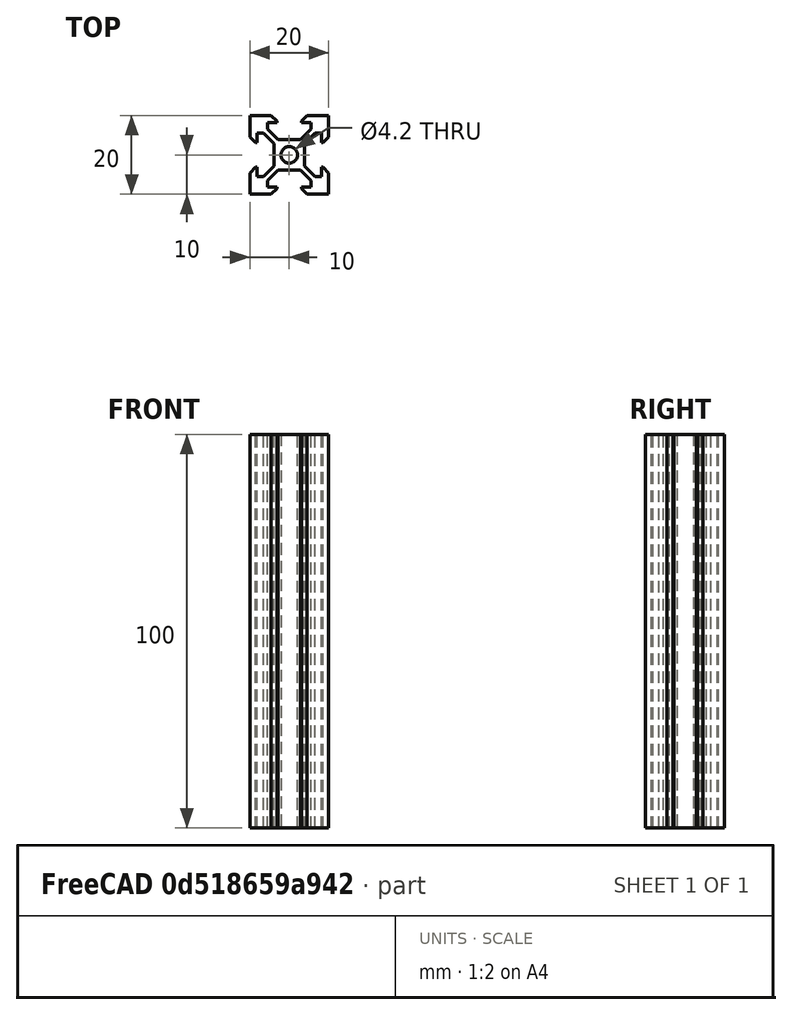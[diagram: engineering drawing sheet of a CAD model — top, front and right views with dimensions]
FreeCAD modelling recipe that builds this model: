
FCSTD DOCUMENT  (FreeCAD 2022.430R26244 +4758 (Git))
Label: V-Slot 2020-100
License: All rights reserved
LicenseURL: http://en.wikipedia.org/wiki/All_rights_reserved
objects: Sketcher::SketchObject×1, PartDesign::Pad×1, PartDesign::Body×1, App::Part×1
note: 5 computed .brp shape members not serialized (recipe doc carries the construction recipe); baked Part::Feature solids carry a one-line shape summary decoded from their .brp

FEATURE [Sketcher::SketchObject] Sketch
  FullyConstrained = true
  MapMode = 5
  Support = -> [XY_Plane001]
  TreeRank = 0
  sketch-geometry (59):
    g0: Circle CenterX=0 CenterY=0 CenterZ=0 NormalX=0 NormalY=0 NormalZ=1 AngleXU=0 Radius=2.1
    g1: LineSegment StartX=-10 StartY=10 StartZ=0 EndX=-4.58 EndY=10 EndZ=0
    g2: LineSegment StartX=10 StartY=10 StartZ=0 EndX=10 EndY=4.58 EndZ=0
    g3: LineSegment StartX=10 StartY=-10 StartZ=0 EndX=4.58 EndY=-10 EndZ=0
    g4: LineSegment StartX=-10 StartY=-10 StartZ=0 EndX=-10 EndY=-4.58 EndZ=0
    g5: LineSegment StartX=-5.5 StartY=6.56066 StartZ=0 EndX=-2.83934 EndY=3.9 EndZ=0
    g6: LineSegment StartX=-6.56066 StartY=5.5 StartZ=0 EndX=-3.9 EndY=2.83934 EndZ=0
    g7: LineSegment StartX=2.83934 StartY=3.9 StartZ=0 EndX=5.5 EndY=6.56066 EndZ=0
    g8: LineSegment StartX=3.9 StartY=2.83934 StartZ=0 EndX=6.56066 EndY=5.5 EndZ=0
    g9: LineSegment StartX=3.9 StartY=-2.83934 StartZ=0 EndX=6.56066 EndY=-5.5 EndZ=0
    g10: LineSegment StartX=2.83934 StartY=-3.9 StartZ=0 EndX=5.5 EndY=-6.56066 EndZ=0
    g11: LineSegment StartX=-2.83934 StartY=-3.9 StartZ=0 EndX=-5.5 EndY=-6.56066 EndZ=0
    g12: LineSegment StartX=-3.9 StartY=-2.83934 StartZ=0 EndX=-6.56066 EndY=-5.5 EndZ=0
    g13: LineSegment [constr] StartX=-10 StartY=10 StartZ=0 EndX=10 EndY=-10 EndZ=0
    g14: LineSegment [constr] StartX=-10 StartY=-10 StartZ=0 EndX=10 EndY=10 EndZ=0
    g15: LineSegment StartX=-2.83934 StartY=3.9 StartZ=0 EndX=2.83934 EndY=3.9 EndZ=0
    g16: LineSegment StartX=-3.9 StartY=2.83934 StartZ=0 EndX=-3.9 EndY=-2.83934 EndZ=0
    g17: LineSegment StartX=-2.83934 StartY=-3.9 StartZ=0 EndX=2.83934 EndY=-3.9 EndZ=0
    g18: LineSegment StartX=3.9 StartY=2.83934 StartZ=0 EndX=3.9 EndY=-2.83934 EndZ=0
    g19: LineSegment StartX=-5.5 StartY=6.56066 StartZ=0 EndX=-5.5 EndY=8.2 EndZ=0
    g20: LineSegment StartX=5.5 StartY=6.56066 StartZ=0 EndX=5.5 EndY=8.2 EndZ=0
    g21: LineSegment StartX=6.56066 StartY=5.5 StartZ=0 EndX=8.2 EndY=5.5 EndZ=0
    g22: LineSegment StartX=6.56066 StartY=-5.5 StartZ=0 EndX=8.2 EndY=-5.5 EndZ=0
    g23: LineSegment StartX=5.5 StartY=-6.56066 StartZ=0 EndX=5.5 EndY=-8.2 EndZ=0
    g24: LineSegment StartX=-5.5 StartY=-6.56066 StartZ=0 EndX=-5.5 EndY=-8.2 EndZ=0
    g25: LineSegment StartX=-6.56066 StartY=-5.5 StartZ=0 EndX=-8.2 EndY=-5.5 EndZ=0
    g26: LineSegment StartX=-6.56066 StartY=5.5 StartZ=0 EndX=-8.2 EndY=5.5 EndZ=0
    g27: LineSegment StartX=-8.2 StartY=-5.5 StartZ=0 EndX=-8.2 EndY=-3.125 EndZ=0
    g28: LineSegment StartX=-8.2 StartY=5.5 StartZ=0 EndX=-8.2 EndY=3.125 EndZ=0
    g29: LineSegment StartX=-5.5 StartY=8.2 StartZ=0 EndX=-3.125 EndY=8.2 EndZ=0
    g30: LineSegment StartX=5.5 StartY=8.2 StartZ=0 EndX=3.125 EndY=8.2 EndZ=0
    g31: LineSegment StartX=8.2 StartY=-5.5 StartZ=0 EndX=8.2 EndY=-3.125 EndZ=0
    g32: LineSegment StartX=8.2 StartY=5.5 StartZ=0 EndX=8.2 EndY=3.125 EndZ=0
    g33: LineSegment StartX=-5.5 StartY=-8.2 StartZ=0 EndX=-3.125 EndY=-8.2 EndZ=0
    g34: LineSegment StartX=5.5 StartY=-8.2 StartZ=0 EndX=3.125 EndY=-8.2 EndZ=0
    g35: LineSegment StartX=-4.58 StartY=10 StartZ=0 EndX=-3.125 EndY=8.545 EndZ=0
    g36: LineSegment StartX=4.58 StartY=10 StartZ=0 EndX=3.125 EndY=8.545 EndZ=0
    g37: LineSegment StartX=-10 StartY=4.58 StartZ=0 EndX=-8.545 EndY=3.125 EndZ=0
    g38: LineSegment StartX=-10 StartY=-4.58 StartZ=0 EndX=-8.545 EndY=-3.125 EndZ=0
    g39: LineSegment StartX=-4.58 StartY=-10 StartZ=0 EndX=-3.125 EndY=-8.545 EndZ=0
    g40: LineSegment StartX=4.58 StartY=-10 StartZ=0 EndX=3.125 EndY=-8.545 EndZ=0
    g41: LineSegment StartX=10 StartY=4.58 StartZ=0 EndX=8.545 EndY=3.125 EndZ=0
    g42: LineSegment StartX=10 StartY=-4.58 StartZ=0 EndX=8.545 EndY=-3.125 EndZ=0
    g43: LineSegment StartX=4.58 StartY=10 StartZ=0 EndX=10 EndY=10 EndZ=0
    g44: LineSegment StartX=10 StartY=-4.58 StartZ=0 EndX=10 EndY=-10 EndZ=0
    g45: LineSegment StartX=-10 StartY=4.58 StartZ=0 EndX=-10 EndY=10 EndZ=0
    g46: LineSegment StartX=-4.58 StartY=-10 StartZ=0 EndX=-10 EndY=-10 EndZ=0
    g47: LineSegment [constr] StartX=-4.58 StartY=10 StartZ=0 EndX=4.58 EndY=10 EndZ=0
    g48: LineSegment [constr] StartX=-10 StartY=4.58 StartZ=0 EndX=-10 EndY=-4.58 EndZ=0
    g49: LineSegment [constr] StartX=10 StartY=4.58 StartZ=0 EndX=10 EndY=-4.58 EndZ=0
    g50: LineSegment [constr] StartX=-4.58 StartY=-10 StartZ=0 EndX=4.58 EndY=-10 EndZ=0
    g51: LineSegment StartX=-3.125 StartY=8.545 StartZ=0 EndX=-3.125 EndY=8.2 EndZ=0
    g52: LineSegment StartX=3.125 StartY=8.545 StartZ=0 EndX=3.125 EndY=8.2 EndZ=0
    g53: LineSegment StartX=-8.545 StartY=3.125 StartZ=0 EndX=-8.2 EndY=3.125 EndZ=0
    g54: LineSegment StartX=-8.545 StartY=-3.125 StartZ=0 EndX=-8.2 EndY=-3.125 EndZ=0
    g55: LineSegment StartX=8.2 StartY=3.125 StartZ=0 EndX=8.545 EndY=3.125 EndZ=0
    g56: LineSegment StartX=8.2 StartY=-3.125 StartZ=0 EndX=8.545 EndY=-3.125 EndZ=0
    g57: LineSegment StartX=-3.125 StartY=-8.2 StartZ=0 EndX=-3.125 EndY=-8.545 EndZ=0
    g58: LineSegment StartX=3.125 StartY=-8.2 StartZ=0 EndX=3.125 EndY=-8.545 EndZ=0
  constraints (153):
    c: Coincident(g0,g-1)
    c: Diameter(g0) = 4.2
    c: Coincident(g43,g2)
    c: Coincident(g44,g3)
    c: Coincident(g46,g4)
    c: Coincident(g45,g1)
    c: Horizontal(g1)
    c: Horizontal(g3)
    c: Vertical(g2)
    c: Vertical(g4)
    c: Symmetric(g1,g44,g0)
    c: DistanceX(g1,g43) = 20
    c: Coincident(g13,g1)
    c: Coincident(g14,g46)
    c: Coincident(g14,g43)
    c: Symmetric(g6,g5,g13)
    c: Symmetric(g6,g5,g13)
    c: Symmetric(g7,g8,g14)
    c: Symmetric(g7,g8,g14)
    c: Symmetric(g9,g10,g13)
    c: Symmetric(g10,g9,g13)
    c: Symmetric(g12,g11,g14)
    c: Symmetric(g12,g11,g14)
    c: Parallel(g5,g13)
    c: Parallel(g7,g14)
    c: Parallel(g9,g13)
    c: Parallel(g11,g14)
    c: Coincident(g15,g5)
    c: Coincident(g15,g7)
    c: Coincident(g16,g6)
    c: Coincident(g16,g12)
    c: Coincident(g17,g11)
    c: Coincident(g17,g10)
    c: Horizontal(g17)
    c: Coincident(g18,g8)
    c: Coincident(g18,g9)
    c: Vertical(g16)
    c: Vertical(g18)
    c: Horizontal(g15)
    c: Equal(g15,g16)
    c: Equal(g16,g17)
    c: Distance(g7,g8) = 1.5
    c: Coincident(g19,g5)
    c: Coincident(g20,g7)
    c: Vertical(g20)
    c: Coincident(g21,g8)
    c: Horizontal(g21)
    c: Coincident(g22,g9)
    c: Horizontal(g22)
    c: Coincident(g23,g10)
    c: Coincident(g24,g11)
    c: Coincident(g25,g12)
    c: Coincident(g26,g6)
    c: Horizontal(g26)
    c: Coincident(g27,g25)
    c: Coincident(g28,g26)
    c: Coincident(g29,g19)
    c: Coincident(g30,g20)
    c: Coincident(g31,g22)
    c: Vertical(g31)
    c: Coincident(g32,g21)
    c: Vertical(g32)
    c: Coincident(g33,g24)
    c: Horizontal(g33)
    c: Horizontal(g29)
    c: Horizontal(g30)
    c: Horizontal(g25)
    c: Coincident(g34,g23)
    c: Horizontal(g34)
    c: Horizontal(g33,g34)
    c: Vertical(g28)
    c: Vertical(g19)
    c: Vertical(g23)
    c: Vertical(g24)
    c: Vertical(g27)
    c: Vertical(g32,g31)
    c: Equal(g26,g19)
    c: Equal(g19,g20)
    c: Equal(g20,g21)
    c: Equal(g21,g22)
    c: Equal(g22,g23)
    c: Equal(g23,g24)
    c: Equal(g28,g29)
    c: Equal(g29,g30)
    c: Equal(g30,g32)
    c: Equal(g32,g31)
    c: Equal(g31,g34)
    c: Equal(g34,g33)
    c: Symmetric(g29,g30,g-2)
    c: Symmetric(g28,g27,g-1)
    c: Symmetric(g39,g40,g-2)
    c: Symmetric(g39,g40,g-2)
    c: Symmetric(g37,g38,g-1)
    c: Symmetric(g37,g38,g-1)
    c: Symmetric(g35,g36,g-2)
    c: Symmetric(g35,g36,g-2)
    c: Symmetric(g41,g42,g-1)
    c: Symmetric(g41,g42,g-1)
    c: Coincident(g1,g35)
    c: Coincident(g2,g41)
    c: PointOnObject(g44,g42)
    c: PointOnObject(g4,g38)
    c: Coincident(g45,g37)
    c: Coincident(g3,g40)
    c: Symmetric(g1,g37,g13)
    c: Coincident(g43,g36)
    c: Horizontal(g43)
    c: Vertical(g44)
    c: Vertical(g45)
    c: PointOnObject(g0,g14)
    c: PointOnObject(g0,g13)
    c: Horizontal(g46)
    c: Angle(g36,g35) = 1.5708
    c: Angle(g37,g38) = 1.5708
    c: Coincident(g39,g46)
    c: Angle(g39,g40) = 1.5708
    c: Angle(g42,g41) = 1.5708
    c: DistanceX(g24,g23) = 11
    c: Coincident(g47,g1)
    c: Coincident(g47,g36)
    c: Coincident(g48,g37)
    c: Coincident(g48,g4)
    c: Coincident(g49,g2)
    c: Coincident(g49,g42)
    c: Coincident(g50,g39)
    c: Coincident(g50,g3)
    c: Equal(g48,g50)
    c: Equal(g50,g49)
    c: Coincident(g51,g35)
    c: Coincident(g51,g29)
    c: Vertical(g51)
    c: Coincident(g52,g36)
    c: Coincident(g52,g30)
    c: Coincident(g53,g37)
    c: Coincident(g53,g28)
    c: Coincident(g54,g38)
    c: Coincident(g54,g27)
    c: Horizontal(g53)
    c: Coincident(g55,g32)
    c: Coincident(g55,g41)
    c: Coincident(g56,g31)
    c: Coincident(g56,g42)
    c: Horizontal(g55)
    c: Coincident(g57,g33)
    c: Coincident(g57,g39)
    c: Coincident(g58,g34)
    c: Coincident(g58,g40)
    c: Vertical(g57)
    c: DistanceX(g39,g40) = 6.25
    c: DistanceY(g3,g23) = 1.8
    c: DistanceY(g34,g10) = 4.3
    c: DistanceX(g50,g50) = 9.16
    c: PointOnObject(g13,g44)
FEATURE [PartDesign::Pad] Pad
  AddSubType = 0
  CheckUpToFaceLimits = true
  ClaimChildren = false
  Direction = (0,0,1)
  Fit = 0
  FitJoin = 0
  InnerFit = 0
  InnerFitJoin = 0
  InnerTaperAngle = 0
  InnerTaperAngleRev = 0
  Length = 100
  Length2 = 100
  NewSolid = false
  Profile = -> Sketch
  Suppress = false
  TreeRank = 0
  Type = 0
  _ProfileBasedVersion = 0
FEATURE [PartDesign::Body] Body  label="VSlot2020_100_Body"
  AutoGroupSolids = false
  ClaimAllChildren = false
  ExportMode = 0
  Group = -> [Sketch,Pad]
  Origin = -> Origin001
  Tip = -> Pad
  TreeRank = 0
  _ExportChildren = -> [Pad]
  _GroupVersion = 1
FEATURE [App::Part] Part  label="V-Slot_2020-100mm"
  ClaimAllChildren = false
  ExportMode = 1
  Group = -> [Body]
  Origin = -> Origin
  TreeRank = 0
  _ExportChildren = -> [Body]
  _GroupVersion = 1
